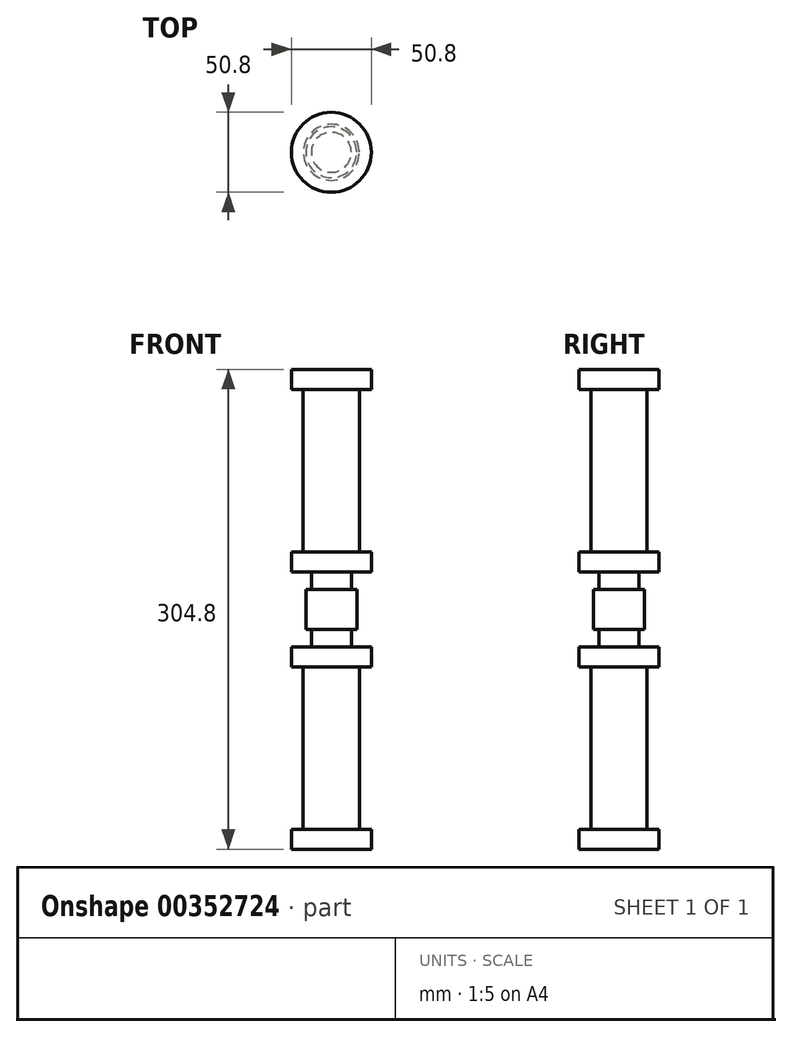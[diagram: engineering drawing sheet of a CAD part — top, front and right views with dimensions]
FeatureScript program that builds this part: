
annotation { "Feature Type Name" : "Feature", "Feature Type Description" : "" }
export const myFeature = defineFeature(function(context is Context, id is Id, definition is map)
    precondition{}
    {
        {
            var Q0;
            Q0=qCreatedBy(makeId("Front.planeOp"),FACE);
            var sketch = newSketch(context, id + "F0", { "sketchPlane" : qUnion([Q0])});
            skLineSegment(sketch, "E0.bottom", {"start": v(-6.35, 152.4) * mm, "end": v(6.35, 152.4) * mm});
            skLineSegment(sketch, "E0.top", {"start": v(-6.35, -152.4) * mm, "end": v(6.35, -152.4) * mm});
            skLineSegment(sketch, "E0.right", {"start": v(6.35, 152.4) * mm, "end": v(6.35, -152.4) * mm});
            skPoint(sketch, "E0.middle", {"position": v(0, 0) * mm});
            skLineSegment(sketch, "E1", {"start": v(-77.73, 0) * mm, "end": v(-9.83, 0) * mm, "construction": true});
            skLineSegment(sketch, "E2.top", {"start": v(-6.35, -12.7) * mm, "end": v(-9.83, -12.7) * mm});
            skLineSegment(sketch, "E2.left", {"start": v(6.35, 0) * mm, "end": v(6.35, -12.7) * mm});
            skLineSegment(sketch, "E2.right", {"start": v(-9.83, 0) * mm, "end": v(-9.83, -12.7) * mm});
            skLineSegment(sketch, "E3.bottom", {"start": v(-6.35, -23.8) * mm, "end": v(-19.05, -23.8) * mm});
            skLineSegment(sketch, "E3.top", {"start": v(-11.45, -36.5) * mm, "end": v(-19.05, -36.5) * mm});
            skLineSegment(sketch, "E3.left", {"start": v(6.35, -23.8) * mm, "end": v(6.35, -36.5) * mm});
            skLineSegment(sketch, "E3.right", {"start": v(-19.05, -23.8) * mm, "end": v(-19.05, -36.5) * mm});
            skLineSegment(sketch, "E4.left", {"start": v(6.35, -36.5) * mm, "end": v(6.35, -139.7) * mm});
            skLineSegment(sketch, "E4.right", {"start": v(-11.45, -36.5) * mm, "end": v(-11.45, -139.7) * mm});
            skPoint(sketch, "E5.oppositeSnap0", {"position": v(0, -152.4) * mm});
            skLineSegment(sketch, "E5.bottom", {"start": v(-11.45, -139.7) * mm, "end": v(-19.05, -139.7) * mm});
            skLineSegment(sketch, "E5.top", {"start": v(6.35, -152.4) * mm, "end": v(-19.05, -152.4) * mm});
            skLineSegment(sketch, "E5.left", {"start": v(6.35, -139.7) * mm, "end": v(6.35, -152.4) * mm});
            skLineSegment(sketch, "E5.right", {"start": v(-19.05, -139.7) * mm, "end": v(-19.05, -152.4) * mm});
            skLineSegment(sketch, "E6.MirrorCS", {"start": v(-9.83, 0) * mm, "end": v(-9.83, 12.7) * mm});
            skLineSegment(sketch, "E7.MirrorCS", {"start": v(-6.35, 12.7) * mm, "end": v(-9.83, 12.7) * mm});
            skLineSegment(sketch, "E8.MirrorCS", {"start": v(-6.35, 23.8) * mm, "end": v(-19.05, 23.8) * mm});
            skLineSegment(sketch, "E9.MirrorCS", {"start": v(-19.05, 23.8) * mm, "end": v(-19.05, 36.5) * mm});
            skLineSegment(sketch, "E10.MirrorCS", {"start": v(-11.45, 36.5) * mm, "end": v(-19.05, 36.5) * mm});
            skLineSegment(sketch, "E11.MirrorCS", {"start": v(-11.45, 36.5) * mm, "end": v(-11.45, 139.7) * mm});
            skLineSegment(sketch, "E12.MirrorCS", {"start": v(-11.45, 139.7) * mm, "end": v(-19.05, 139.7) * mm});
            skLineSegment(sketch, "E13.MirrorCS", {"start": v(-19.05, 139.7) * mm, "end": v(-19.05, 152.4) * mm});
            skLineSegment(sketch, "E14.MirrorCS", {"start": v(6.35, 152.4) * mm, "end": v(-19.05, 152.4) * mm});
            skLineSegment(sketch, "E15.trimOffspring", {"start": v(-6.35, -12.7) * mm, "end": v(-6.35, -23.8) * mm});
            skLineSegment(sketch, "E16.trimOffspring", {"start": v(6.35, 0) * mm, "end": v(75.57, 0) * mm, "construction": true});
            skPoint(sketch, "E17.orphan", {"position": v(6.35, 12.7) * mm});
            skPoint(sketch, "E18.orphan", {"position": v(6.35, 23.8) * mm});
            skLineSegment(sketch, "E19.trimOffspring", {"start": v(-6.35, 23.8) * mm, "end": v(-6.35, 12.7) * mm});
            skPoint(sketch, "E20.orphan", {"position": v(6.35, 36.5) * mm});
            skPoint(sketch, "E21.orphan", {"position": v(6.35, 139.7) * mm});
            skSolve(sketch);
        }
        {
            var Q0;
            Q0=qSketchRegion(id+"F0",true);
            var Q1;
            Q1=sQuery(id+"F0.wireOp",EDGE,"E0.right");
            revolve(context, id + "F1", {"entities" : qUnion([Q0]), "axis" : qUnion([Q1]), "revolveType" : RevolveType.FULL});
        }
    });
